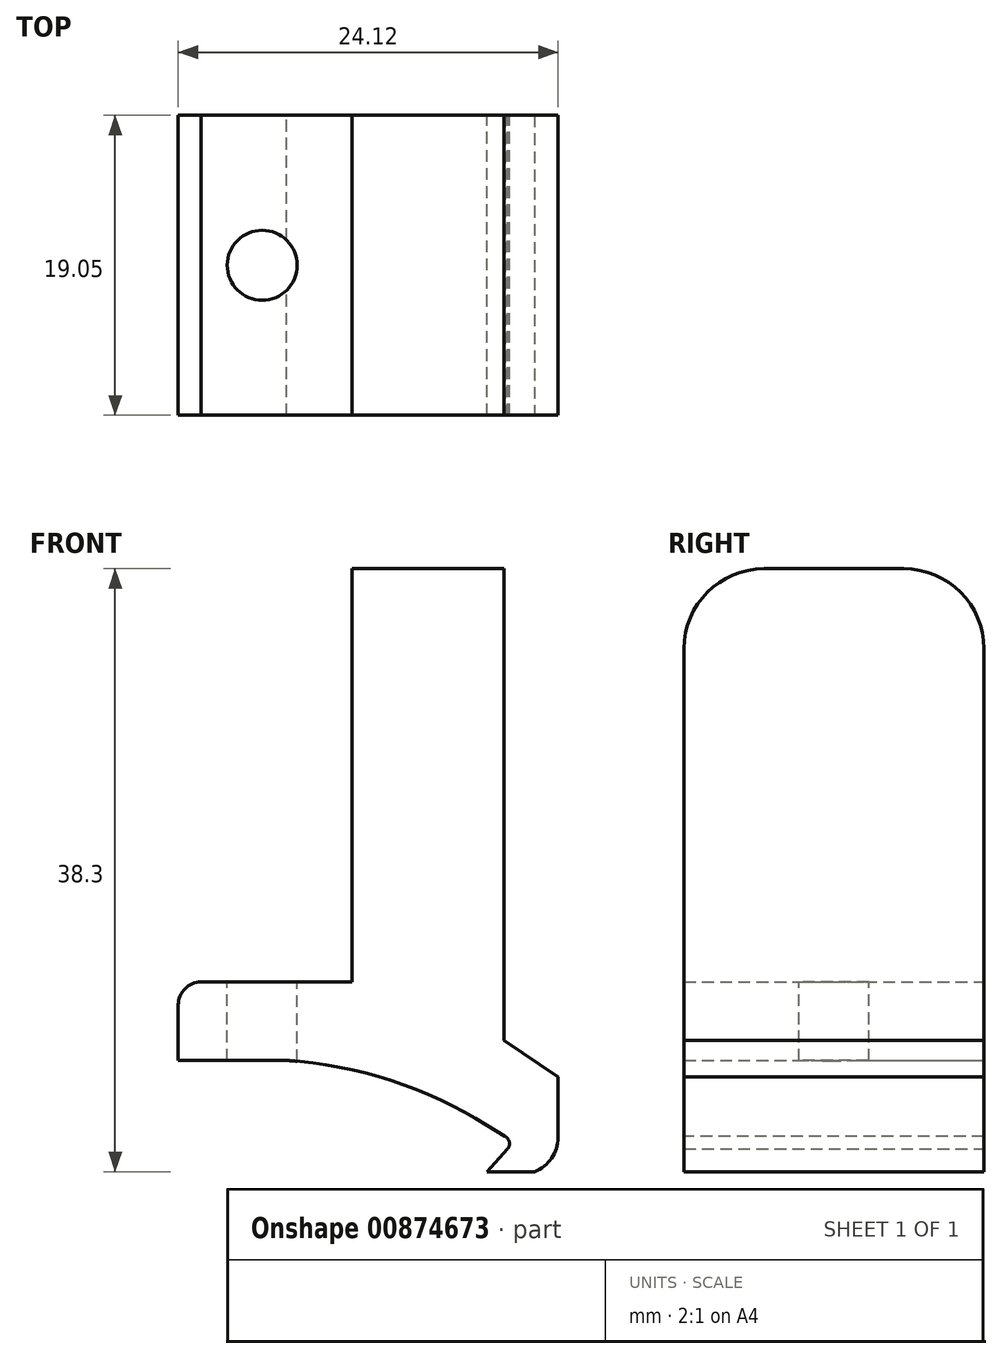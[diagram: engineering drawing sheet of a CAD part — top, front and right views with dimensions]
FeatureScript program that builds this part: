
annotation { "Feature Type Name" : "Feature", "Feature Type Description" : "" }
export const myFeature = defineFeature(function(context is Context, id is Id, definition is map)
    precondition{}
    {
        {
            var Q0;
            Q0=qCreatedBy(makeId("Front.planeOp"),FACE);
            var sketch = newSketch(context, id + "F0", { "sketchPlane" : qUnion([Q0])});
            skLineSegment(sketch, "E0", {"start": v(-12.06, -12.09) * mm, "end": v(-5.19, -12.09) * mm});
            skArc(sketch, "E1", {"start": v(-5.19, -12.09) * mm, "mid": v(1.44, -13.36) * mm, "end": v(7.56, -16.2) * mm});
            skLineSegment(sketch, "E2", {"start": v(7.56, -16.2) * mm, "end": v(8.69, -16.9) * mm});
            skArc(sketch, "E3", {"start": v(8.69, -16.9) * mm, "mid": v(8.96, -17.26) * mm, "end": v(8.86, -17.71) * mm});
            skLineSegment(sketch, "E4", {"start": v(8.86, -17.71) * mm, "end": v(7.56, -19.15) * mm});
            skLineSegment(sketch, "E5", {"start": v(7.56, -19.15) * mm, "end": v(10.58, -19.15) * mm});
            skArc(sketch, "E6", {"start": v(10.58, -19.15) * mm, "mid": v(11.65, -18.3) * mm, "end": v(12.06, -16.98) * mm});
            skLineSegment(sketch, "E7", {"start": v(12.06, -16.98) * mm, "end": v(12.06, -13.14) * mm});
            skLineSegment(sketch, "E8", {"start": v(12.06, -13.14) * mm, "end": v(8.63, -10.82) * mm});
            skLineSegment(sketch, "E9", {"start": v(8.63, -10.82) * mm, "end": v(8.63, 19.15) * mm});
            skLineSegment(sketch, "E10", {"start": v(8.63, 19.15) * mm, "end": v(-1.03, 19.15) * mm});
            skLineSegment(sketch, "E11", {"start": v(-1.03, 19.15) * mm, "end": v(-1.03, -7.1) * mm});
            skLineSegment(sketch, "E12", {"start": v(-1.03, -7.1) * mm, "end": v(-10.62, -7.1) * mm});
            skArc(sketch, "E13", {"start": v(-10.62, -7.1) * mm, "mid": v(-11.64, -7.54) * mm, "end": v(-12.06, -8.56) * mm});
            skLineSegment(sketch, "E14", {"start": v(-12.06, -8.56) * mm, "end": v(-12.06, -12.09) * mm});
            skSolve(sketch);
        }
        {
            var Q0;
            Q0=makeQuery(id+"F0.imprint","IMPRINT",FACE,{"disambiguationData":[TD([[makeQuery(id+"F0.imprint","IMPRINT",EDGE,{"derivedFrom":sQuery(id+"F0.wireOp",EDGE,"E0")}),1.0]])]});
            extrude(context, id + "F1", {"entities" : qUnion([Q0]), "depth" : 19.05 * mm, "offsetDistance" : 25.4 * mm});
        }
        {
            var Q0;
            Q0=makeQuery(id+"F1.opExtrude","CAP_EDGE",EDGE,{"disambiguationData":[OSD([sQuery(id+"F0.wireOp",EDGE,"E10")])],"isStart":false});
            var Q1;
            Q1=makeQuery(id+"F1.opExtrude","CAP_EDGE",EDGE,{"disambiguationData":[OSD([sQuery(id+"F0.wireOp",EDGE,"E10")])],"isStart":true});
            fillet(context, id + "F2", {"entities" : qUnion([Q0, Q1]), "radius" : 5.08 * mm, "tangentPropagation" : true, "allowEdgeOverflow" : false});
        }
        {
            var Q0;
            Q0=makeQuery(id+"F1.opExtrude","SWEPT_FACE",FACE,{"disambiguationData":[OSD([sQuery(id+"F0.wireOp",EDGE,"E12")])]});
            var sketch = newSketch(context, id + "F3", { "sketchPlane" : qUnion([Q0])});
            skCircle(sketch, "E15", {"center": v(-6.73, -9.53) * mm, "radius": 2.22 * mm});
            skSolve(sketch);
        }
        {
            var Q0;
            Q0=makeQuery(id+"F3.imprint","IMPRINT",FACE,{"disambiguationData":[TD([[makeQuery(id+"F3.imprint","IMPRINT",EDGE,{"derivedFrom":sQuery(id+"F3.wireOp",EDGE,"E15")}),1.0]])]});
            extrude(context, id + "F4", {"entities" : qUnion([Q0]), "operationType" : NewBodyOperationType.REMOVE, "endBound" : BoundingType.THROUGH_ALL, "oppositeDirection" : true, "depth" : 25.4 * mm, "offsetDistance" : 25.4 * mm});
        }
    });
